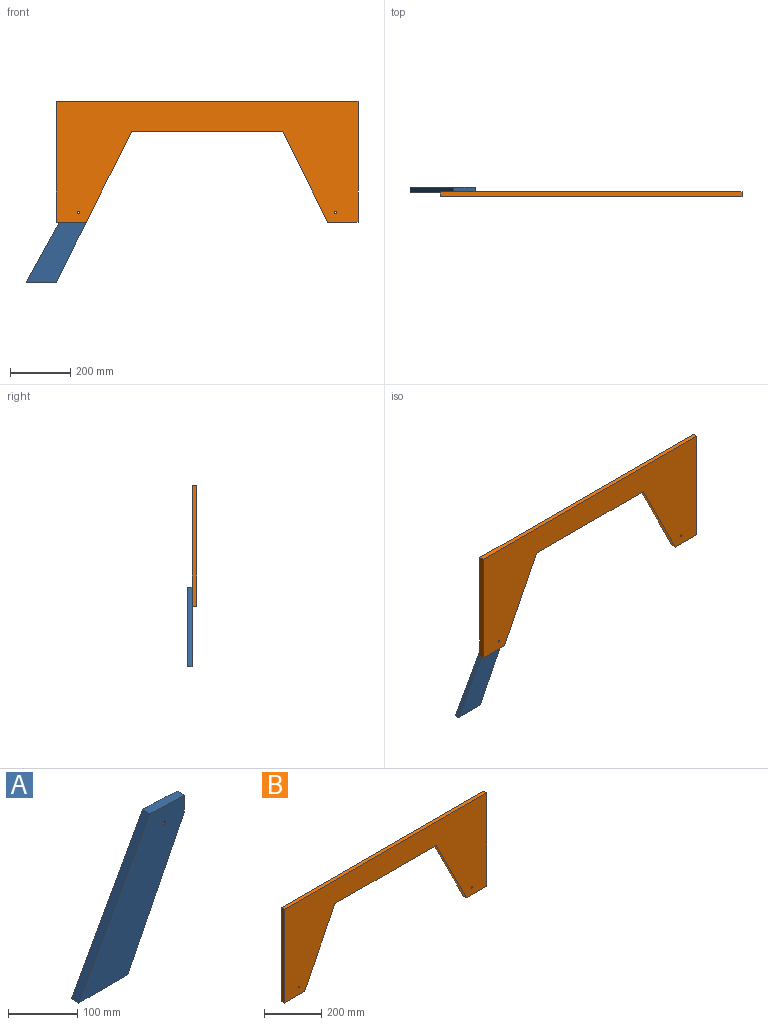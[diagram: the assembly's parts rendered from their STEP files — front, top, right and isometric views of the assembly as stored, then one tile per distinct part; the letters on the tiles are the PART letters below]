
ASSEMBLY  parts=2 mates=1
PART A: 8 faces, bbox 215.9x15x262.3 mm
  f0: plane 231.79x115.9mm, normal (0.89,0,-0.45), area 3887.2mm2, adj f1,f4,f6,f7
  f1: plane 27.93x15mm, normal (1,0,0), area 418.9mm2, adj f0,f2,f6,f7
  f2: plane 70.65x15mm, normal (0.04,0,1), area 1060.4mm2, adj f1,f3,f6,f7
  f3: plane 262.29x145.25mm, normal (-0.87,0,0.48), area 4497.3mm2, adj f2,f4,f6,f7
  f4: plane 100x15mm, normal (0,0,-1), area 1500mm2, adj f0,f3,f6,f7
  f5: cylinder r=3.5mm len=15mm, axis (0,1,0), area 329.9mm2, adj f6,f7
  f6: plane 262.29x215.9mm, normal (0,-1,0), area 24018.1mm2, adj f0,f1,f2,f3,f4,f5
  f7: plane 262.29x215.9mm, normal (0,1,0), area 24018.1mm2, adj f0,f1,f2,f3,f4,f5
PART B: 12 faces, bbox 1000x15x400 mm
  f0: plane 100x15mm, normal (0,0,-1), area 1500mm2, adj f1,f7,f10,f11
  f1: plane 400x15mm, normal (1,0,0), area 6000mm2, adj f0,f2,f10,f11
  f2: plane 1000x15mm, normal (0,0,1), area 15000mm2, adj f1,f3,f10,f11
  f3: plane 400x15mm, normal (-1,0,0), area 6000mm2, adj f2,f4,f10,f11
  f4: plane 100x15mm, normal (0,0,-1), area 1500mm2, adj f3,f5,f10,f11
  f5: plane 300x150mm, normal (0.89,0,-0.45), area 5031.2mm2, adj f4,f6,f10,f11
  f6: plane 500x15mm, normal (0,0,-1), area 7500mm2, adj f5,f7,f10,f11
  f7: plane 300x150mm, normal (-0.89,0,-0.45), area 5031.2mm2, adj f0,f6,f10,f11
  f8: cylinder r=3.5mm len=15mm, axis (0,-1,0), area 329.9mm2, adj f10,f11
  f9: cylinder r=3.5mm len=15mm, axis (0,-1,0), area 329.9mm2, adj f10,f11
  f10: plane 1000x400mm, normal (0,1,0), area 204923mm2, adj f0,f1,f2,f3,f4,f5,f6,f7
  f11: plane 1000x400mm, normal (0,-1,0), area 204923mm2, adj f0,f1,f2,f3,f4,f5,f6,f7
PLACE A t=(-300.99,-58.04,-97.65)mm
PLACE B t=(-300.99,-88.04,-97.65)mm fixed
MATE revolute B.f9 <-> A.f5  axis (0,1,0) through (-227.48,-73.04,-465.86)mm
